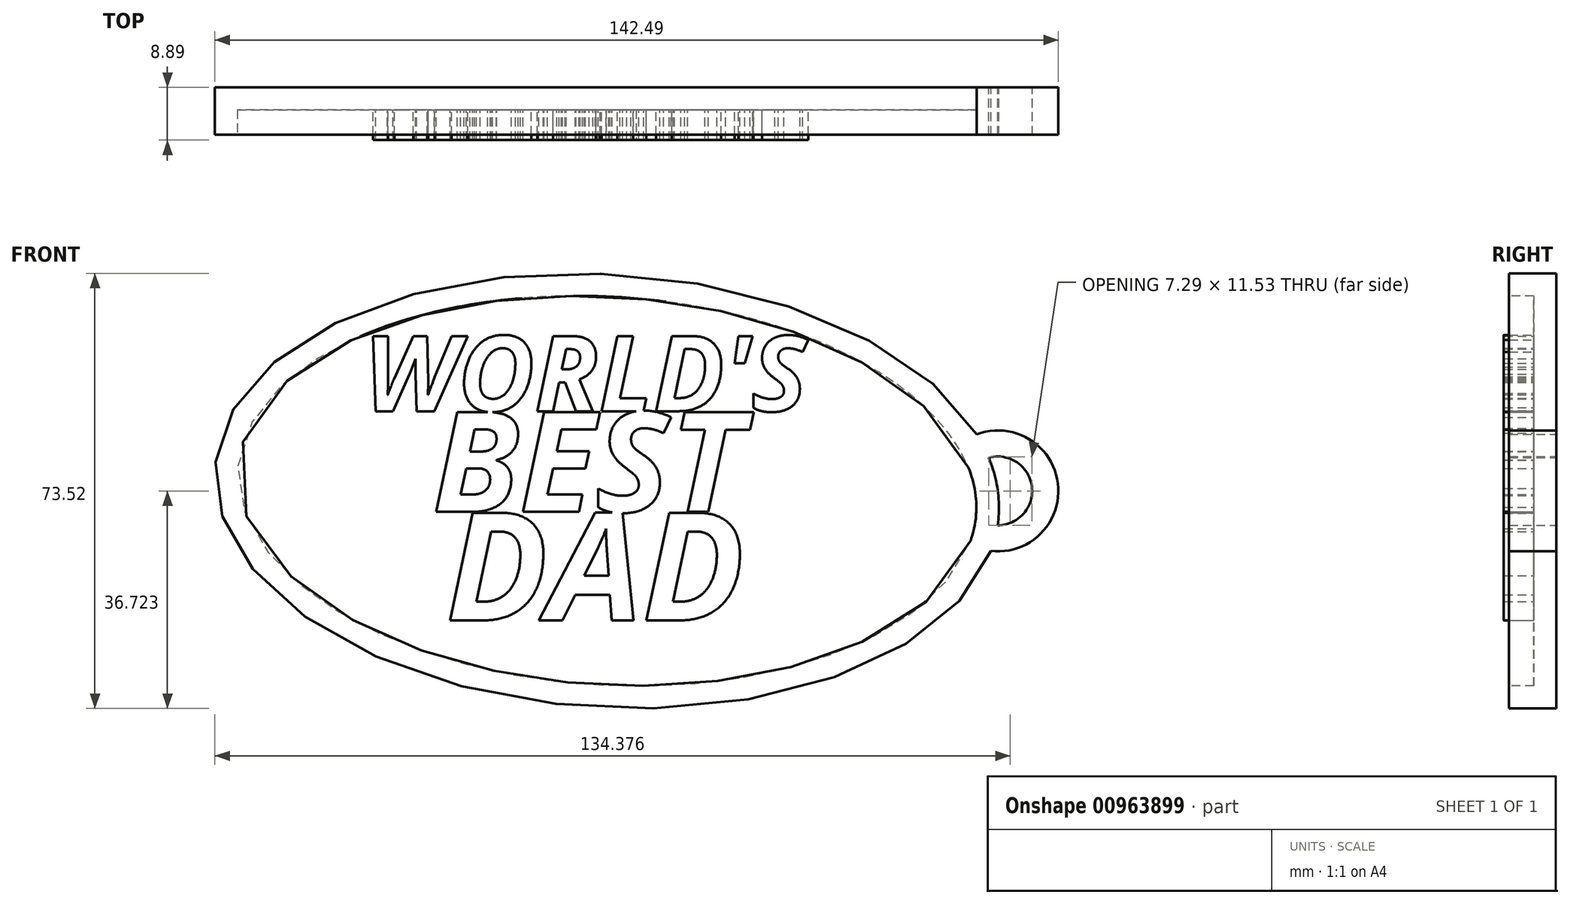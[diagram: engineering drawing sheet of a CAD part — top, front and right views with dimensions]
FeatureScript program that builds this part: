
annotation { "Feature Type Name" : "Feature", "Feature Type Description" : "" }
export const myFeature = defineFeature(function(context is Context, id is Id, definition is map)
    precondition{}
    {
        {
            var Q0;
            Q0=qCreatedBy(makeId("Front.planeOp"),FACE);
            var sketch = newSketch(context, id + "F0", { "sketchPlane" : qUnion([Q0])});
            skEllipse(sketch, "E0", {"center": v(0, 0) * mm, "majorRadius": 66.31 * mm, "minorRadius": 36.61 * mm, "majorAxis": v(1, -0.06)});
            skArc(sketch, "E1", {"start": v(64.86, -10.15) * mm, "mid": v(76.18, 1.24) * mm, "end": v(62.45, 9.57) * mm});
            skArc(sketch, "E2", {"start": v(66, -5.8) * mm, "mid": v(71.8, 0.76) * mm, "end": v(64.5, 5.6) * mm});
            skSolve(sketch);
        }
        {
            var Q0;
            Q0=qSketchRegion(id+"F0",true);
            extrude(context, id + "F1", {"entities" : qUnion([Q0]), "depth" : 8 * mm, "offsetDistance" : 25.4 * mm});
        }
        {
            var Q0;
            Q0=makeQuery(id+"F1.opExtrude","CAP_FACE",FACE,{"disambiguationData":[OSD([sQuery(id+"F0.wireOp",EDGE,"E0"),sQuery(id+"F0.wireOp",EDGE,"E1"),sQuery(id+"F0.wireOp",EDGE,"E2")])],"isStart":false});
            shell(context, id + "F2", {"entities" : qUnion([Q0]), "thickness" : 3.8 * mm});
        }
        {
            var Q0;
            Q0=qCreatedBy(makeId("Front.planeOp"),FACE);
            var sketch = newSketch(context, id + "F3", { "sketchPlane" : qUnion([Q0])});
            skText(sketch, "E3", { "text": "WORLD\'S", "fontName": "OpenSans-BoldItalic.ttf"});
            skText(sketch, "E4", { "text": "BEST", "fontName": "OpenSans-BoldItalic.ttf"});
            skText(sketch, "E5", { "text": "DAD\n", "fontName": "OpenSans-BoldItalic.ttf"});
            const initialGuessF3  = {"E3": [-0.04109, 0.01346, 1, 0, 0.0128], "E4": [-0.02945, -0.00355, 1, 0, 0.01702], "E5": [-0.02718, -0.02188, 1, 0, 0.01832]};
            skSetInitialGuess(sketch, initialGuessF3);
            skSolve(sketch);
        }
        {
            var Q0;
            Q0=qSketchRegion(id+"F3",true);
            extrude(context, id + "F4", {"entities" : qUnion([Q0]), "operationType" : NewBodyOperationType.ADD, "depth" : 8.9 * mm, "offsetDistance" : 25.4 * mm});
        }
    });
